# Revit family: Table-Teknion-CFTFFV_Figure_Table_Rectangular_Open_V_Leg_Flat_Edge-R2023
name_source: partatom
category: Furniture
units: mm (PartAtom-declared; Revit-internal decimal feet)

## family parameters
Always vertical = Yes
Cut with Voids When Loaded = No
Enable Cutting in Views = No
OmniClass Number = 23.40.20.00
OmniClass Title = General Furniture and Specialties
Render Appearance Source = Family Geometry
Room Calculation Point = No
Shared = Yes
Work Plane-Based = No

## types (1)
- Figure Table, Rectangular, Open V Leg, Flat Edge
    Assembly Code = E2020200
    Default Elevation = 0 "
    Description = Figure Table, Rectangular, Open V Leg, Flat Edge
    Manufacturer = Teknion
    Manufacturer Fax = 416.661.4586
    Model = CFTFFV_________
    Part Number = CFTFFV
    Product Documentation Link = https://d2r72yk5wmppdj.cloudfront.net
    Product Line = Figure Table
    Product Page URL = https://www.teknion.com
    Series = Custom Wood
    Sustainability Data = https://www.teknion.com
    URL = www.teknion.com
    Unit Weight URL = http://www.teknion.com
    Warranty = http://www.teknion.com

## geometry (parser evidence)
native form markers: Sweep x14
no freeform markers — native parametric forms only
